# Revit family: RL-1 Return Valve Angle Model 3724
name_source: partatom
category: Rohrzubehör
units: mm (PartAtom-declared; Revit-internal decimal feet)

## family parameters
Arbeitsebenenbasiert = Nein
Beim Laden mit Abzugskörper schneiden = Nein
Bemaßung runder Anschluss = Durchmesser verwenden
Gemeinsam genutzt = Nein
Immer vertikal = Nein
OmniClass-Nummer = 23.65.55.14
OmniClass-Titel = Valves for Liquid Services
Teiletyp = Unterbricht

## types (1)
- RL-1 Return Valve Angle Model 3724
    Application = Hot Water Heating Systems
After installation of the return valve it is possible to close the radiator return connection.
When the intake valve is closed simultaneously (0-position for thermostatic valves) it is possible to remove the radiator while the heating system remains under pressure.
Thus, it is possible to perform servicing operations and to work behind the radiator (wall-papering, laying tiles) without having to switch off the rest of the system.
If presetting of the return valve or filling and draining of the radiators or of the entire system through the return valve is required, we recommend using the HERZ-RL-5 return valve.
    Body = nickel-plated
    H04 = 25.5 mm
    H05 = 5.2 mm  [stored 0.0170604 ft]
    Hersteller = HERZ Armaturen Ges.m.b.H.
    Max. operating pressure = 1000000.0 Pa
    Max. operating temperature = 110 °C
    Medium = Hot water purity according to Austrian standard ÖNORM H 5195 and/or VDI guideline 2035.
    Model = All models are nickel-plated and are universal models with special socket for threaded pipe and compression union.
    R01 = 10.5 mm  [stored 0.0344488 ft]
    R06 = 11 mm  [stored 0.0360892 ft]
    S01 = 10 mm  [stored 0.0328084 ft]
    S04 = 45 mm
    SCRNCODE = 05;01;02
    SCRNSEQ = ARM;ARM_TYP="ALLF";2
    URL = www.herzvalves.com
    Vorgabe-Ansicht = 0 mm  [stored 0 ft]

note: [stored X ft] marks values corroborated as IEEE doubles in the binary element streams (Revit-internal decimal feet)
